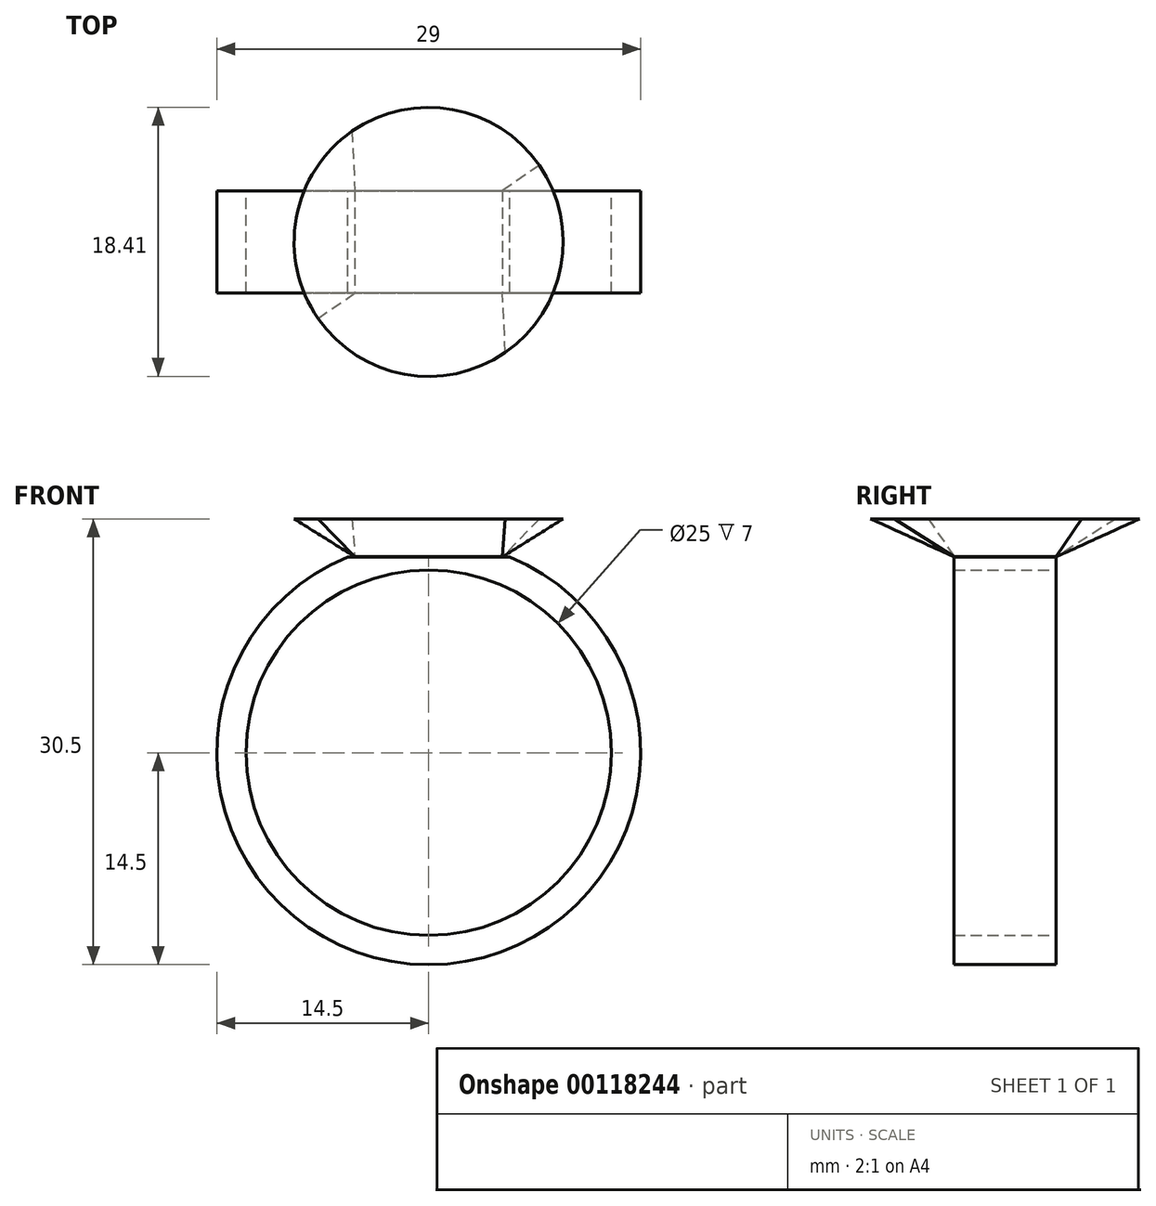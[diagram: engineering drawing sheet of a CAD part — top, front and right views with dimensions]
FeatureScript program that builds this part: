
annotation { "Feature Type Name" : "Feature", "Feature Type Description" : "" }
export const myFeature = defineFeature(function(context is Context, id is Id, definition is map)
    precondition{}
    {
        {
            var Q0;
            Q0=qCreatedBy(makeId("Front.planeOp"),FACE);
            var sketch = newSketch(context, id + "F0", { "sketchPlane" : qUnion([Q0])});
            skCircle(sketch, "E0", {"center": v(0, 0) * mm, "radius": 14.5 * mm});
            skCircle(sketch, "E1", {"center": v(0, 0) * mm, "radius": 12.5 * mm});
            skSolve(sketch);
        }
        {
            var Q0;
            Q0=makeQuery(id+"F0.imprint","IMPRINT",FACE,{"disambiguationData":[TD([[makeQuery(id+"F0.imprint","IMPRINT",EDGE,{"derivedFrom":sQuery(id+"F0.wireOp",EDGE,"E0")}),1.0]])]});
            extrude(context, id + "F1", {"entities" : qUnion([Q0]), "depth" : 7 * mm});
        }
        {
            var Q0;
            Q0=qCreatedBy(makeId("Front.planeOp"),FACE);
            var sketch = newSketch(context, id + "F2", { "sketchPlane" : qUnion([Q0])});
            skLineSegment(sketch, "E2.bottom", {"start": v(-16.96, 17.45) * mm, "end": v(31.23, 17.45) * mm});
            skLineSegment(sketch, "E2.top", {"start": v(-16.96, 13.4) * mm, "end": v(31.23, 13.4) * mm});
            skLineSegment(sketch, "E2.left", {"start": v(-16.96, 17.45) * mm, "end": v(-16.96, 13.4) * mm});
            skLineSegment(sketch, "E2.right", {"start": v(31.23, 17.45) * mm, "end": v(31.23, 13.4) * mm});
            skSolve(sketch);
        }
        {
            var Q0;
            Q0=makeQuery(id+"F2.imprint","IMPRINT",FACE,{"disambiguationData":[TD([[makeQuery(id+"F2.imprint","IMPRINT",EDGE,{"derivedFrom":sQuery(id+"F2.wireOp",EDGE,"E2.bottom")}),-1.0]])]});
            extrude(context, id + "F3", {"entities" : qUnion([Q0]), "operationType" : NewBodyOperationType.REMOVE, "depth" : 28 * mm});
        }
        {
            var Q0;
            Q0=qCreatedBy(makeId("Top.planeOp"),FACE);
            cPlane(context, id + "F4", {"entities" : qUnion([Q0]), "cplaneType" : CPlaneType.OFFSET, "offset" : 13.4 * mm, "width" : 150 * mm, "height" : 150 * mm});
        }
        {
            var Q0;
            Q0=qCreatedBy(id+"F4.planeOp",FACE);
            var sketch = newSketch(context, id + "F5", { "sketchPlane" : qUnion([Q0])});
            skLineSegment(sketch, "E3.bottom", {"start": v(5.05, 0) * mm, "end": v(-5.05, 0) * mm});
            skLineSegment(sketch, "E3.top", {"start": v(5.05, -7) * mm, "end": v(-5.05, -7) * mm});
            skLineSegment(sketch, "E3.left", {"start": v(5.05, 0) * mm, "end": v(5.05, -7) * mm});
            skLineSegment(sketch, "E3.right", {"start": v(-5.05, 0) * mm, "end": v(-5.05, -7) * mm});
            skSolve(sketch);
        }
        {
            var Q0;
            Q0=qCreatedBy(makeId("Top.planeOp"),FACE);
            cPlane(context, id + "F6", {"entities" : qUnion([Q0]), "cplaneType" : CPlaneType.OFFSET, "offset" : 16 * mm, "width" : 150 * mm, "height" : 150 * mm});
        }
        {
            var Q0;
            Q0=qCreatedBy(id+"F6.planeOp",FACE);
            var sketch = newSketch(context, id + "F7", { "sketchPlane" : qUnion([Q0])});
            skCircle(sketch, "E4", {"center": v(0, -3.5) * mm, "radius": 9.2 * mm});
            skSolve(sketch);
        }
        {
            var Q0;
            Q0=makeQuery(id+"F7.imprint","IMPRINT",FACE,{"disambiguationData":[TD([[makeQuery(id+"F7.imprint","IMPRINT",EDGE,{"derivedFrom":sQuery(id+"F7.wireOp",EDGE,"E4")}),1.0]])]});
            var Q1;
            Q1=makeQuery(id+"F5.imprint","IMPRINT",FACE,{"disambiguationData":[TD([[makeQuery(id+"F5.imprint","IMPRINT",EDGE,{"derivedFrom":sQuery(id+"F5.wireOp",EDGE,"E3.bottom")}),1.0]])]});
            loft(context, id + "F8", {"sheetProfilesArray" : [{ "sheetProfileEntities" : qUnion([Q0]) }, { "sheetProfileEntities" : qUnion([Q1]) }]});
        }
    });
